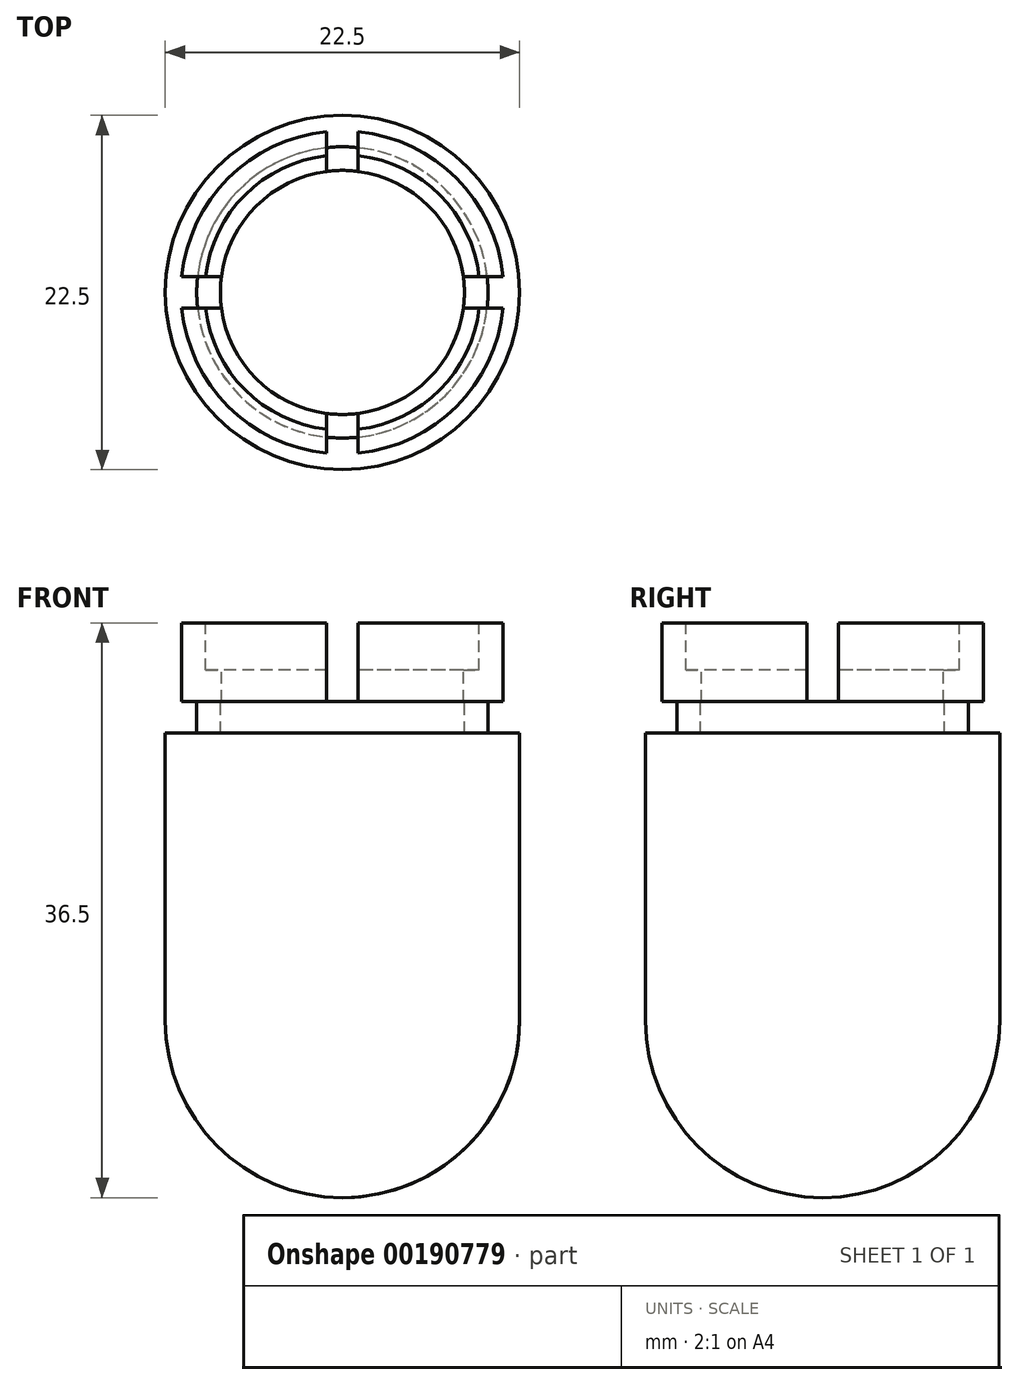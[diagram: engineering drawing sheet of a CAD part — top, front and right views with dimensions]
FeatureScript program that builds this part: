
annotation { "Feature Type Name" : "Feature", "Feature Type Description" : "" }
export const myFeature = defineFeature(function(context is Context, id is Id, definition is map)
    precondition{}
    {
        {
            var Q0;
            Q0=qCreatedBy(makeId("Front.planeOp"),FACE);
            var sketch = newSketch(context, id + "F0", { "sketchPlane" : qUnion([Q0])});
            skLineSegment(sketch, "E0.left", {"start": v(11.25, 18.75) * mm, "end": v(11.25, 0) * mm});
            skPoint(sketch, "E0.middle", {"position": v(0, 0) * mm});
            skPoint(sketch, "E1.visualSharp", {"position": v(11.25, 30) * mm});
            skArc(sketch, "E1.filletArc", {"start": v(11.25, 18.75) * mm, "mid": v(7.95, 26.7) * mm, "end": v(0, 30) * mm, "construction": true});
            skPoint(sketch, "E2", {"position": v(11.25, 0) * mm});
            skPoint(sketch, "E3", {"position": v(0, 30) * mm});
            skPoint(sketch, "E0.right.start.orphan", {"position": v(-11.25, 30) * mm});
            skPoint(sketch, "E0.top.end.orphan", {"position": v(-11.25, -30) * mm});
            skPoint(sketch, "E4.orphan", {"position": v(11.25, -30) * mm});
            skPoint(sketch, "E5", {"position": v(11.25, 0.5) * mm});
            skLineSegment(sketch, "E6", {"start": v(11.25, 0.5) * mm, "end": v(10.25, 0.5) * mm, "construction": true});
            skLineSegment(sketch, "E7", {"start": v(10.25, 0.5) * mm, "end": v(10.25, 0) * mm});
            skLineSegment(sketch, "E8", {"start": v(10.25, 0) * mm, "end": v(10.25, -0.5) * mm, "construction": true});
            skArc(sketch, "E9.0", {"start": v(10.25, 18.75) * mm, "mid": v(7.25, 26) * mm, "end": v(0, 29) * mm, "construction": true});
            skLineSegment(sketch, "E9.1", {"start": v(10.25, 18.75) * mm, "end": v(10.25, 1.5) * mm, "construction": true});
            skPoint(sketch, "E10", {"position": v(11.25, 1.5) * mm});
            skLineSegment(sketch, "E11", {"start": v(10.25, 1.5) * mm, "end": v(9.25, 1.5) * mm});
            skLineSegment(sketch, "E12", {"start": v(9.25, 1.5) * mm, "end": v(9.25, -0.5) * mm});
            skLineSegment(sketch, "E13", {"start": v(9.25, -0.5) * mm, "end": v(10.25, -0.5) * mm});
            skLineSegment(sketch, "E14", {"start": v(0, 30) * mm, "end": v(0, 29) * mm});
            skLineSegment(sketch, "E15.trimOffspring", {"start": v(10.25, 0.5) * mm, "end": v(10.25, 0) * mm, "construction": true});
            skLineSegment(sketch, "E16.bottom", {"start": v(0, 30.9) * mm, "end": v(0, 30.9) * mm});
            skLineSegment(sketch, "E16.top", {"start": v(0, 35.9) * mm, "end": v(0, 35.9) * mm});
            skLineSegment(sketch, "E16.left", {"start": v(1.5, 32.4) * mm, "end": v(1.5, 34.4) * mm});
            skLineSegment(sketch, "E16.right", {"start": v(-1.5, 32.4) * mm, "end": v(-1.5, 34.4) * mm});
            skPoint(sketch, "E16.middle", {"position": v(0, 33.4) * mm});
            skLineSegment(sketch, "E17", {"start": v(-11.25, 30) * mm, "end": v(11.25, 30) * mm, "construction": true});
            skLineSegment(sketch, "E18", {"start": v(-11.25, 30) * mm, "end": v(-11.25, -30) * mm, "construction": true});
            skLineSegment(sketch, "E19", {"start": v(11.25, 30) * mm, "end": v(11.25, -0.5) * mm, "construction": true});
            skPoint(sketch, "E20.visualSharp", {"position": v(1.5, 35.9) * mm});
            skArc(sketch, "E20.filletArc", {"start": v(1.5, 34.4) * mm, "mid": v(1.06, 35.46) * mm, "end": v(0, 35.9) * mm});
            skPoint(sketch, "E21.visualSharp", {"position": v(1.5, 30.9) * mm});
            skArc(sketch, "E21.filletArc", {"start": v(0, 30.9) * mm, "mid": v(1.06, 31.34) * mm, "end": v(1.5, 32.4) * mm});
            skPoint(sketch, "E22.visualSharp", {"position": v(-1.5, 30.9) * mm});
            skArc(sketch, "E22.filletArc", {"start": v(-1.5, 32.4) * mm, "mid": v(-1.06, 31.34) * mm, "end": v(0, 30.9) * mm});
            skPoint(sketch, "E23.visualSharp", {"position": v(-1.5, 35.9) * mm});
            skArc(sketch, "E23.filletArc", {"start": v(0, 35.9) * mm, "mid": v(-1.06, 35.46) * mm, "end": v(-1.5, 34.4) * mm});
            skLineSegment(sketch, "E24.0", {"start": v(2.3, 32.4) * mm, "end": v(2.3, 34.4) * mm});
            skArc(sketch, "E24.1", {"start": v(0, 36.7) * mm, "mid": v(-1.63, 36.03) * mm, "end": v(-2.3, 34.4) * mm});
            skLineSegment(sketch, "E24.2", {"start": v(-2.3, 32.4) * mm, "end": v(-2.3, 34.4) * mm});
            skArc(sketch, "E24.3", {"start": v(2.3, 34.4) * mm, "mid": v(1.63, 36.03) * mm, "end": v(0, 36.7) * mm});
            skArc(sketch, "E24.4", {"start": v(-2.3, 32.4) * mm, "mid": v(-1.63, 30.78) * mm, "end": v(0, 30.1) * mm});
            skArc(sketch, "E24.5", {"start": v(0, 30.1) * mm, "mid": v(1.63, 30.78) * mm, "end": v(2.3, 32.4) * mm});
            skLineSegment(sketch, "E25", {"start": v(0, 33.4) * mm, "end": v(2.3, 33.4) * mm, "construction": true});
            skLineSegment(sketch, "E26", {"start": v(0, 33.4) * mm, "end": v(-2.3, 33.4) * mm, "construction": true});
            skLineSegment(sketch, "E27.bottom", {"start": v(0.4, 30.3) * mm, "end": v(-0.4, 30.3) * mm});
            skLineSegment(sketch, "E27.top", {"start": v(0.4, 29.8) * mm, "end": v(-0.4, 29.8) * mm});
            skLineSegment(sketch, "E27.left", {"start": v(0.4, 30.3) * mm, "end": v(0.4, 29.8) * mm});
            skLineSegment(sketch, "E27.right", {"start": v(-0.4, 30.3) * mm, "end": v(-0.4, 29.8) * mm});
            skPoint(sketch, "E27.middle", {"position": v(0, 30.06) * mm});
            skLineSegment(sketch, "E28", {"start": v(10.25, 6.5) * mm, "end": v(-11.25, 6.5) * mm, "construction": true});
            skLineSegment(sketch, "E29", {"start": v(8.75, 6.5) * mm, "end": v(8.75, 3.5) * mm});
            skLineSegment(sketch, "E30", {"start": v(8.75, 3.5) * mm, "end": v(7.75, 3.5) * mm});
            skLineSegment(sketch, "E31", {"start": v(7.75, 3.5) * mm, "end": v(7.75, -0.5) * mm});
            skLineSegment(sketch, "E32", {"start": v(7.75, -0.5) * mm, "end": v(11.25, -0.5) * mm});
            skLineSegment(sketch, "E33", {"start": v(10.25, 6.5) * mm, "end": v(8.75, 6.5) * mm});
            skLineSegment(sketch, "E34", {"start": v(7.75, -0.5) * mm, "end": v(0, -0.5) * mm});
            skLineSegment(sketch, "E35", {"start": v(11.25, -0.5) * mm, "end": v(11.25, -18.75) * mm});
            skLineSegment(sketch, "E36", {"start": v(0, -30) * mm, "end": v(0, -30) * mm});
            skArc(sketch, "E37.filletArc", {"start": v(0, -30) * mm, "mid": v(7.95, -26.7) * mm, "end": v(11.25, -18.75) * mm});
            skLineSegment(sketch, "E38", {"start": v(0, -0.5) * mm, "end": v(0, -30) * mm});
            skLineSegment(sketch, "E39", {"start": v(10.25, 6.5) * mm, "end": v(10.25, 1.5) * mm});
            skLineSegment(sketch, "E40", {"start": v(0, -0.5) * mm, "end": v(1, -0.5) * mm});
            skLineSegment(sketch, "E41", {"start": v(1, 1.5) * mm, "end": v(1, 6.5) * mm});
            skLineSegment(sketch, "E42", {"start": v(1, 6.5) * mm, "end": v(0, 6.5) * mm});
            skLineSegment(sketch, "E43.MirrorCS", {"start": v(-8.25, 6.5) * mm, "end": v(13.25, 6.5) * mm, "construction": true});
            skLineSegment(sketch, "E44.MirrorCS", {"start": v(-1, 1.5) * mm, "end": v(-1, 6.5) * mm});
            skLineSegment(sketch, "E45", {"start": v(-1, 6.5) * mm, "end": v(1, 6.5) * mm});
            skLineSegment(sketch, "E46", {"start": v(1, 1.5) * mm, "end": v(-1, 1.5) * mm});
            skPoint(sketch, "E46.startSnap0", {"position": v(7.75, 1.5) * mm});
            skPoint(sketch, "E47.orphan", {"position": v(-1, -0.5) * mm});
            skPoint(sketch, "E48.MirrorCS.start.orphan", {"position": v(0, -0.5) * mm});
            skSolve(sketch);
        }
        {
            var Q0;
            Q0=qCreatedBy(makeId("Top.planeOp"),FACE);
            var sketch = newSketch(context, id + "F1", { "sketchPlane" : qUnion([Q0])});
            skCircle(sketch, "E49", {"center": v(0, 0) * mm, "radius": 11.25 * mm});
            skSolve(sketch);
        }
        {
            var Q0;
            {var subQ0=sQuery(id+"F0.wireOp",EDGE,"E34");Q0=makeQuery(id+"F0.imprint","IMPRINT",FACE,{"disambiguationData":[TD([[makeQuery(id+"F0.imprint","IMPRINT",EDGE,{"derivedFrom":subQ0}),1.0]])]});}
            var Q1;
            Q1=makeQuery(id+"F0.imprint","IMPRINT",FACE,{"disambiguationData":[TD([[makeQuery(id+"F0.imprint","IMPRINT",EDGE,{"derivedFrom":sQuery(id+"F0.wireOp",EDGE,"E11")}),-1.0]])]});
            var Q2;
            Q2=sQuery(id+"F1.wireOp",EDGE,"E49");
            sweep(context, id + "F2", {"profiles" : qUnion([Q0, Q1]), "path" : qUnion([Q2])});
        }
        {
            var Q0;
            {var subQ1=sQuery(id+"F0.wireOp",EDGE,"E41");Q0=makeQuery(id+"F0.imprint","IMPRINT",FACE,{"disambiguationData":[TD([[makeQuery(id+"F0.imprint","IMPRINT",EDGE,{"derivedFrom":subQ1}),1.0]])]});}
            extrude(context, id + "F3", {"entities" : qUnion([Q0]), "operationType" : NewBodyOperationType.REMOVE, "oppositeDirection" : true, "depth" : 25 * mm, "hasSecondDirection" : true, "secondDirectionOppositeDirection" : false, "secondDirectionDepth" : 25 * mm});
        }
        {
            var Q0;
            Q0=qCreatedBy(makeId("Right.planeOp"),FACE);
            var sketch = newSketch(context, id + "F4", { "sketchPlane" : qUnion([Q0])});
            skLineSegment(sketch, "E50", {"start": v(0, 1.5) * mm, "end": v(-1, 1.5) * mm});
            skLineSegment(sketch, "E51", {"start": v(-1, 1.5) * mm, "end": v(-1, 6.5) * mm});
            skLineSegment(sketch, "E52", {"start": v(-1, 6.5) * mm, "end": v(1, 6.5) * mm});
            skLineSegment(sketch, "E53", {"start": v(1, 6.5) * mm, "end": v(1, 1.5) * mm});
            skLineSegment(sketch, "E54", {"start": v(1, 1.5) * mm, "end": v(0, 1.5) * mm});
            skSolve(sketch);
        }
        {
            var Q0;
            Q0=makeQuery(id+"F4.imprint","IMPRINT",FACE,{"disambiguationData":[TD([[makeQuery(id+"F4.imprint","IMPRINT",EDGE,{"derivedFrom":sQuery(id+"F4.wireOp",EDGE,"E50")}),-1.0]])]});
            extrude(context, id + "F5", {"entities" : qUnion([Q0]), "operationType" : NewBodyOperationType.REMOVE, "oppositeDirection" : true, "depth" : 25 * mm, "hasSecondDirection" : true, "secondDirectionOppositeDirection" : false, "secondDirectionDepth" : 25 * mm});
        }
    });
